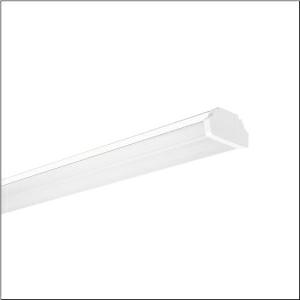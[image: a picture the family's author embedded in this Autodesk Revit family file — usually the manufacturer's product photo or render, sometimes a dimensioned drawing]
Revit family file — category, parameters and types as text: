
# Revit family: dus_31_gen_2_53bd812cv675c2_3805
name_source: partatom
category: Lighting Fixtures
units: mm (PartAtom-declared; Revit-internal decimal feet)

## family parameters
Cut with Voids When Loaded = No
Host = Face
Light Source = No
Part Type = Normal
Room Calculation Point = No
Round Connector Dimension = Use Diameter
Shared = No

## types (1)
- --- (1 x LED, 7670 lm, 42.1 W, 6500K)
    Apparent Load = 42 VA
    CIE Flux Codes = 47 80 95 93 100
    Color Rendering = 80
    Color Temperature = 6500K
    Default Elevation = 1800 mm
    Description = DUS 31 Gen.2, luminaire insert, of sheet steel, coil coated, white, length: 1.535mm, width: 81mm, height: 90mm, 5x system unit, system units: 307mm, LED rated luminous flux: 7.670lm, light colour: 865, SDCM (Standard Deviation of Colour Matching)MacAdam ≤ 3 SDCM (initial), control gear: ON/OFF Multilumen, CLOi, with plug, 3-pole, with phase selection, mains connection: 220..240V, AC, 50/60Hz, start of lifetime: 42W, end of service life: 50W, through-wiring accessed according to module size, primary optical cover: cover, of PMMA, light emission: direct distribution, primary light characteristic: symmetric, protection rating (complete): IP20, protection rating (LED compartment): IP50, insulation class (complete): insulation class I (protective earthing), certification: CE, ENEC, VDE, UKCA, impact resistance: IK03, permissible ambient temperature for indoor applications: -35..+50°C, corresponds to IFS (International Featured Standards) requirements for safety and quality in the food industry, reducing of maximum allowable ambient temperature of 5°C with ceiling mounting, packaging unit: 1 piece
    Height = 95 mm
    Lamp = 1 x LED
    Lamp Light Flux = 7670 lm
    Lamp Power = 42.1 W
    Lamp count = 1
    Length = 1535 mm
    Luminous efficacy = 182 lm/W
    Manufacturer = Siteco
    ModVariant = No
    Model = 53BD812CV675C2
    Mounting Place = Ceiling
    Mounting Type = Pendant
    Number of Poles = 1
    OnlyDefault = Yes
    Power Factor = 1
    Product Name = DUS 31 Gen.2
    Product group = luminaire insert | ceiling pendant
    ProductGroupID = 901
    Protection Class = Protection class I
    Protection Degree = IP 20
    RLX_Detail_Level = 1
    RLX_Emergency_Light_Flux = 0 lm
    RLX_Emergency_Type = 0
    RLX_Emergency_Type_DB = No
    RlxData = <blob elided: 29877 chars, md5=acb90db7>
    Socket = socket
    Standby Power = 0 W
    System Light Flux = 7670 lm
    System Power = 42 W
    Type Comments = factory setting: luminous flux: 100 % | (A | C | E) | 98 mA
    Type Image = l_1319596.jpg
    URL = http://relux.com
    VarID = @adj_042365
    Voltage = 0 V
    Weight = 0.00 kg
    Width = 81 mm

## geometry (parser evidence)
native form markers: Blend x4, Sweep x14
no freeform markers — native parametric forms only
